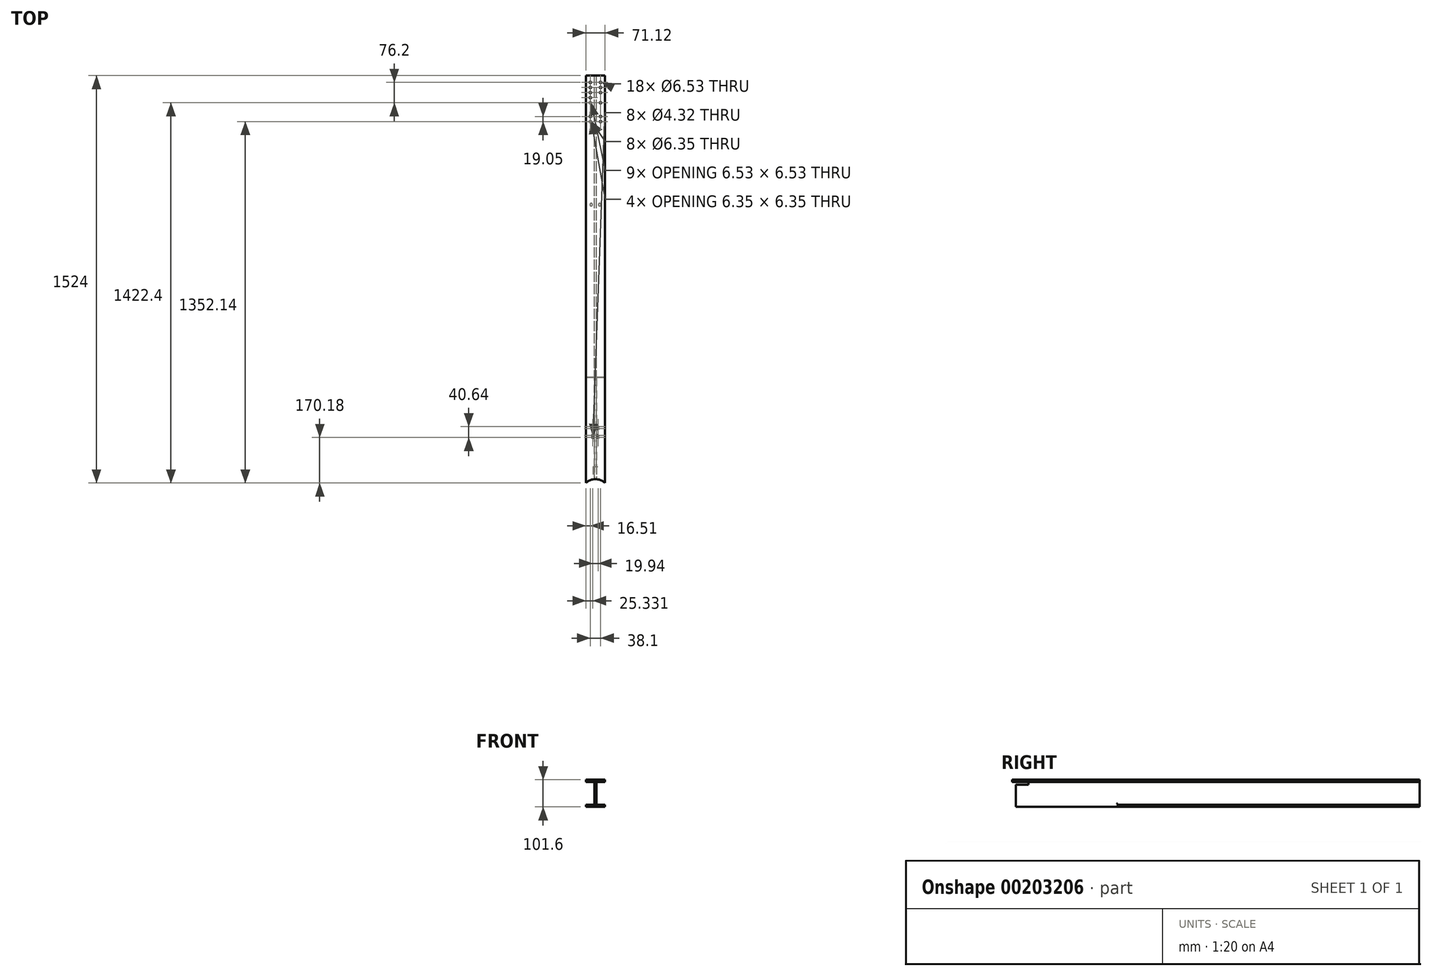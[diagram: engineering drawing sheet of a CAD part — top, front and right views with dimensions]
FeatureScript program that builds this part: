
annotation { "Feature Type Name" : "Feature", "Feature Type Description" : "" }
export const myFeature = defineFeature(function(context is Context, id is Id, definition is map)
    precondition{}
    {
        {
            var Q0;
            Q0=qCreatedBy(makeId("Front.planeOp"),FACE);
            var sketch = newSketch(context, id + "F0", { "sketchPlane" : qUnion([Q0])});
            skLineSegment(sketch, "E0.bottom", {"start": v(35.56, -50.8) * mm, "end": v(-35.56, -50.8) * mm});
            skLineSegment(sketch, "E0.top", {"start": v(35.56, 50.8) * mm, "end": v(-35.56, 50.8) * mm});
            skLineSegment(sketch, "E0.left", {"start": v(35.56, -50.8) * mm, "end": v(35.56, -42.42) * mm});
            skLineSegment(sketch, "E0.right", {"start": v(-35.56, -50.8) * mm, "end": v(-35.56, -42.42) * mm});
            skPoint(sketch, "E0.middle", {"position": v(0, 0) * mm});
            skLineSegment(sketch, "E1", {"start": v(-35.56, 50.8) * mm, "end": v(-35.56, 42.42) * mm});
            skLineSegment(sketch, "E2", {"start": v(-35.56, 42.42) * mm, "end": v(-4.2, 42.42) * mm});
            skLineSegment(sketch, "E3", {"start": v(0, 50.8) * mm, "end": v(-4.2, 50.8) * mm});
            skLineSegment(sketch, "E4", {"start": v(-4.2, 42.42) * mm, "end": v(-4.2, 0) * mm});
            skLineSegment(sketch, "E5.MirrorCS", {"start": v(4.2, 42.42) * mm, "end": v(4.2, 0) * mm});
            skLineSegment(sketch, "E6.MirrorCS", {"start": v(35.56, 50.8) * mm, "end": v(35.56, 42.42) * mm});
            skLineSegment(sketch, "E7.MirrorCS", {"start": v(-35.56, -42.42) * mm, "end": v(-4.2, -42.42) * mm});
            skLineSegment(sketch, "E8.MirrorCS", {"start": v(-4.2, -42.42) * mm, "end": v(-4.2, 0) * mm});
            skLineSegment(sketch, "E9.MirrorCS", {"start": v(4.2, -42.42) * mm, "end": v(4.2, 0) * mm});
            skPoint(sketch, "E10.orphan", {"position": v(0, -50.8) * mm});
            skLineSegment(sketch, "E11.trimOffspring", {"start": v(4.2, -42.42) * mm, "end": v(35.56, -42.42) * mm});
            skLineSegment(sketch, "E12.trimOffspring", {"start": v(4.2, 42.42) * mm, "end": v(35.56, 42.42) * mm});
            skLineSegment(sketch, "E13.trimOffspring", {"start": v(35.56, 42.42) * mm, "end": v(35.56, 50.8) * mm});
            skLineSegment(sketch, "E14.trimOffspring", {"start": v(-35.56, 42.42) * mm, "end": v(-35.56, 50.8) * mm});
            skSolve(sketch);
        }
        {
            var Q0;
            Q0=makeQuery(id+"F0.imprint","IMPRINT",FACE,{"disambiguationData":[TD([[makeQuery(id+"F0.imprint","IMPRINT",EDGE,{"derivedFrom":sQuery(id+"F0.wireOp",EDGE,"E0.bottom")}),-1.0]])]});
            extrude(context, id + "F1", {"entities" : qUnion([Q0]), "depth" : 1524 * mm});
        }
        {
            var Q0;
            Q0=makeQuery(id+"F1.opExtrude","SWEPT_EDGE",EDGE,{"disambiguationData":[OSD([sQuery(id+"F0.wireOp",EDGE,"E5.MirrorCS"),sQuery(id+"F0.wireOp",EDGE,"E12.trimOffspring")])]});
            var Q1;
            Q1=makeQuery(id+"F1.opExtrude","SWEPT_EDGE",EDGE,{"disambiguationData":[OSD([sQuery(id+"F0.wireOp",EDGE,"E9.MirrorCS"),sQuery(id+"F0.wireOp",EDGE,"E11.trimOffspring")])]});
            var Q2;
            Q2=makeQuery(id+"F1.opExtrude","SWEPT_EDGE",EDGE,{"disambiguationData":[OSD([sQuery(id+"F0.wireOp",EDGE,"E7.MirrorCS"),sQuery(id+"F0.wireOp",EDGE,"E8.MirrorCS")])]});
            var Q3;
            Q3=makeQuery(id+"F1.opExtrude","SWEPT_EDGE",EDGE,{"disambiguationData":[OSD([sQuery(id+"F0.wireOp",EDGE,"E2"),sQuery(id+"F0.wireOp",EDGE,"E4")])]});
            fillet(context, id + "F2", {"entities" : qUnion([Q0, Q1, Q2, Q3]), "radius" : 5.08 * mm, "tangentPropagation" : true, "allowEdgeOverflow" : false});
        }
        {
            var Q0;
            Q0=makeQuery(id+"F1.opExtrude","SWEPT_FACE",FACE,{"disambiguationData":[OSD([sQuery(id+"F0.wireOp",EDGE,"E0.top"),sQuery(id+"F0.wireOp",EDGE,"E3")])]});
            var sketch = newSketch(context, id + "F3", { "sketchPlane" : qUnion([Q0])});
            skLineSegment(sketch, "E15", {"start": v(0, -1524) * mm, "end": v(0, -1560.28) * mm});
            skPoint(sketch, "E15.endSnap0", {"position": v(0, -1524) * mm});
            skLineSegment(sketch, "E16", {"start": v(35.56, -1524) * mm, "end": v(0, -1560.28) * mm});
            skCircle(sketch, "E17", {"center": v(0, -1560.28) * mm, "radius": 50.8 * mm});
            skLineSegment(sketch, "E18.trimOffspring", {"start": v(0, -1611.08) * mm, "end": v(0, -1676.71) * mm});
            skSolve(sketch);
        }
        {
            var Q0;
            {var subQ6=sQuery(id+"F3.wireOp",EDGE,"E15");Q0=makeQuery(id+"F3.imprint","IMPRINT",FACE,{"disambiguationData":[TD([[makeQuery(id+"F3.imprint","IMPRINT",EDGE,{"derivedFrom":subQ6}),-1.0]])]});}
            var Q1;
            {var subQ0=sQuery(id+"F3.wireOp",EDGE,"E15");Q1=makeQuery(id+"F3.imprint","IMPRINT",FACE,{"disambiguationData":[TD([[makeQuery(id+"F3.imprint","IMPRINT",EDGE,{"derivedFrom":subQ0}),1.0]])]});}
            var Q2;
            {var subQ1=sQuery(id+"F0.wireOp",EDGE,"E0.top");var subQ2=makeQuery(id+"F1.opExtrude","CAP_EDGE",EDGE,{"disambiguationData":[OSD([subQ1,sQuery(id+"F0.wireOp",EDGE,"E3")])],"isStart":false});var subQ5=makeQuery(id+"F3.imprint","INTERSECT",VERTEX,{"derivedFrom":[subQ2,sQuery(id+"F3.wireOp",EDGE,"E15")]});Q2=makeQuery(id+"F3.imprint","IMPRINT",FACE,{"disambiguationData":[TD([[makeQuery(id+"F3.imprint","IMPRINT",EDGE,{"disambiguationData":[TD([[subQ5,-1.0]])],"derivedFrom":subQ2}),-1.0]])]});}
            extrude(context, id + "F4", {"entities" : qUnion([Q0, Q1, Q2]), "operationType" : NewBodyOperationType.REMOVE, "oppositeDirection" : true, "depth" : 101.6 * mm});
        }
        {
            var Q0;
            Q0=makeQuery(id+"F1.opExtrude","SWEPT_FACE",FACE,{"disambiguationData":[OSD([sQuery(id+"F0.wireOp",EDGE,"E5.MirrorCS"),sQuery(id+"F0.wireOp",EDGE,"E9.MirrorCS")])]});
            var sketch = newSketch(context, id + "F5", { "sketchPlane" : qUnion([Q0])});
            skSolve(sketch);
        }
        {
            var Q0;
            {var subQ0=sQuery(id+"F0.wireOp",EDGE,"E9.MirrorCS");var subQ1=sQuery(id+"F0.wireOp",EDGE,"E5.MirrorCS");Q0=makeQuery(id+"F5.imprint","IMPRINT",FACE,{"disambiguationData":[TD([[makeQuery(id+"F5.imprint","IMPRINT",EDGE,{"derivedFrom":makeQuery(id+"F1.opExtrude","CAP_EDGE",EDGE,{"disambiguationData":[OSD([subQ1,subQ0])],"isStart":true})}),1.0]])]});}
            var sketch = newSketch(context, id + "F6", { "sketchPlane" : qUnion([Q0])});
            skLineSegment(sketch, "E19", {"start": v(-1510.33, 42.42) * mm, "end": v(-1510.33, 32.26) * mm});
            skLineSegment(sketch, "E20", {"start": v(-1510.33, 32.26) * mm, "end": v(-1462.07, 32.26) * mm});
            skLineSegment(sketch, "E21", {"start": v(-1462.07, 32.26) * mm, "end": v(-1462.07, 42.42) * mm});
            skLineSegment(sketch, "E22", {"start": v(-1462.07, 42.42) * mm, "end": v(-1510.33, 42.42) * mm});
            skSolve(sketch);
        }
        {
            var Q0;
            Q0=qSketchRegion(id+"F6",true);
            extrude(context, id + "F7", {"entities" : qUnion([Q0]), "operationType" : NewBodyOperationType.REMOVE, "oppositeDirection" : true, "depth" : 25.4 * mm, "symmetric" : true});
        }
        {
            var Q0;
            Q0=makeQuery(id+"F7.boolean.opBoolean","INTERSECT",EDGE,{"derivedFrom":[makeQuery(id+"F4.boolean.opBoolean","COPY",FACE,{"derivedFrom":makeQuery(id+"F4.opExtrude","SWEPT_FACE",FACE,{"disambiguationData":[OSD([sQuery(id+"F3.wireOp",EDGE,"E17")])]})}),makeQuery(id+"F7.opExtrude","SWEPT_FACE",FACE,{"disambiguationData":[OSD([sQuery(id+"F6.wireOp",EDGE,"E20")])]})]});
            chamfer(context, id + "F8", {"entities" : qUnion([Q0]), "width" : 1.27 * mm, "tangentPropagation" : true});
        }
        {
            var Q0;
            Q0=makeQuery(id+"F1.opExtrude","SWEPT_FACE",FACE,{"disambiguationData":[OSD([sQuery(id+"F0.wireOp",EDGE,"E0.top"),sQuery(id+"F0.wireOp",EDGE,"E3")])]});
            var sketch = newSketch(context, id + "F9", { "sketchPlane" : qUnion([Q0])});
            skLineSegment(sketch, "E23", {"start": v(-0.26, -1524) * mm, "end": v(-0.26, -0.03) * mm});
            skLineSegment(sketch, "E24.bottom", {"start": v(9.71, -1353.82) * mm, "end": v(-10.23, -1353.82) * mm});
            skLineSegment(sketch, "E24.top", {"start": v(9.71, -1313.18) * mm, "end": v(-10.23, -1313.18) * mm});
            skLineSegment(sketch, "E25.bottom", {"start": v(9.71, -1346.2) * mm, "end": v(-10.23, -1346.2) * mm});
            skLineSegment(sketch, "E25.top", {"start": v(9.71, -1320.8) * mm, "end": v(-10.23, -1320.8) * mm});
            skLineSegment(sketch, "E26", {"start": v(35.56, -1524) * mm, "end": v(-35.56, -1524) * mm});
            skLineSegment(sketch, "E27", {"start": v(-0.26, -1524) * mm, "end": v(-0.26, -1353.82) * mm});
            skLineSegment(sketch, "E28", {"start": v(-0.26, -1353.82) * mm, "end": v(-0.26, -1346.2) * mm});
            skLineSegment(sketch, "E29", {"start": v(-0.26, -1346.2) * mm, "end": v(-0.26, -1320.8) * mm});
            skLineSegment(sketch, "E30", {"start": v(-0.26, -1320.8) * mm, "end": v(-0.26, -1313.18) * mm});
            skSolve(sketch);
        }
        {
            var Q0;
            Q0=sQuery(id+"F9.wireOp",VERTEX,"E24.bottom.end");
            var Q1;
            Q1=sQuery(id+"F9.wireOp",VERTEX,"E25.bottom.end");
            var Q2;
            Q2=sQuery(id+"F9.wireOp",VERTEX,"E25.top.end");
            var Q3;
            Q3=sQuery(id+"F9.wireOp",VERTEX,"E24.top.end");
            var Q4;
            Q4=sQuery(id+"F9.wireOp",VERTEX,"E24.top.start");
            var Q5;
            Q5=sQuery(id+"F9.wireOp",VERTEX,"E25.top.start");
            var Q6;
            Q6=sQuery(id+"F9.wireOp",VERTEX,"E25.bottom.start");
            var Q7;
            Q7=sQuery(id+"F9.wireOp",VERTEX,"E24.bottom.start");
            var Q8;
            Q8=makeQuery(id+"F1.opExtrude","SWEPT_BODY",BODY,{"disambiguationData":[OSD([sQuery(id+"F0.wireOp",EDGE,"E0.bottom"),sQuery(id+"F0.wireOp",EDGE,"E0.top"),sQuery(id+"F0.wireOp",EDGE,"E0.left"),sQuery(id+"F0.wireOp",EDGE,"E0.right"),sQuery(id+"F0.wireOp",EDGE,"E2"),sQuery(id+"F0.wireOp",EDGE,"E3"),sQuery(id+"F0.wireOp",EDGE,"E4"),sQuery(id+"F0.wireOp",EDGE,"E5.MirrorCS"),sQuery(id+"F0.wireOp",EDGE,"E7.MirrorCS"),sQuery(id+"F0.wireOp",EDGE,"E8.MirrorCS"),sQuery(id+"F0.wireOp",EDGE,"E9.MirrorCS"),sQuery(id+"F0.wireOp",EDGE,"E11.trimOffspring"),sQuery(id+"F0.wireOp",EDGE,"E12.trimOffspring"),sQuery(id+"F0.wireOp",EDGE,"E13.trimOffspring"),sQuery(id+"F0.wireOp",EDGE,"E14.trimOffspring")])]});
            hole(context, id + "F10", {"style" : HoleStyle.SIMPLE, "endStyle" : HoleEndStyle.BLIND, "standardTappedOrClearance" : lookupTablePath({ "standard" : "ANSI", "fit" : "Close", "size" : "#8", "type" : "Clearance" }), "standardBlindInLast" : lookupTablePath({ "fit" : "Close", "standard" : "ANSI", "size" : "#8", "type" : "Clearance" }), "holeDiameter" : 4.32 * mm, "holeDepth" : 25.4 * mm, "locations" : qUnion([Q0, Q1, Q2, Q3, Q4, Q5, Q6, Q7]), "scope" : qUnion([Q8])});
        }
        {
            var Q0;
            Q0=makeQuery(id+"F1.opExtrude","SWEPT_FACE",FACE,{"disambiguationData":[OSD([sQuery(id+"F0.wireOp",EDGE,"E0.bottom")])]});
            var sketch = newSketch(context, id + "F11", { "sketchPlane" : qUnion([Q0])});
            skLineSegment(sketch, "E31", {"start": v(4.2, 1509.65) * mm, "end": v(4.2, 1128.65) * mm});
            skLineSegment(sketch, "E32.bottom", {"start": v(4.2, 1128.65) * mm, "end": v(39.68, 1128.65) * mm});
            skLineSegment(sketch, "E32.top", {"start": v(4.2, 1528.41) * mm, "end": v(39.68, 1528.41) * mm});
            skLineSegment(sketch, "E32.left", {"start": v(4.2, 1128.65) * mm, "end": v(4.2, 1528.41) * mm});
            skLineSegment(sketch, "E32.right", {"start": v(39.68, 1128.65) * mm, "end": v(39.68, 1528.41) * mm});
            skLineSegment(sketch, "E33", {"start": v(0, 1526.52) * mm, "end": v(0, 1517.43) * mm});
            skLineSegment(sketch, "E34.MirrorCS", {"start": v(-4.2, 1528.41) * mm, "end": v(-39.68, 1528.41) * mm});
            skLineSegment(sketch, "E35.MirrorCS", {"start": v(-39.68, 1128.65) * mm, "end": v(-39.68, 1528.41) * mm});
            skLineSegment(sketch, "E36.MirrorCS", {"start": v(-4.2, 1128.65) * mm, "end": v(-4.2, 1528.41) * mm});
            skLineSegment(sketch, "E37.MirrorCS", {"start": v(-4.2, 1128.65) * mm, "end": v(-39.68, 1128.65) * mm});
            skSolve(sketch);
        }
        {
            var Q0;
            Q0=qSketchRegion(id+"F11",true);
            extrude(context, id + "F12", {"entities" : qUnion([Q0]), "operationType" : NewBodyOperationType.REMOVE, "oppositeDirection" : true, "depth" : 25.4 * mm});
        }
        {
            var Q0;
            Q0=makeQuery(id+"F12.boolean.opBoolean","COPY",EDGE,{"derivedFrom":makeQuery(id+"F12.opExtrude","SWEPT_EDGE",EDGE,{"disambiguationData":[OSD([sQuery(id+"F11.wireOp",EDGE,"E32.bottom"),sQuery(id+"F11.wireOp",EDGE,"E32.left")])]})});
            var Q1;
            Q1=makeQuery(id+"F12.boolean.opBoolean","COPY",EDGE,{"derivedFrom":makeQuery(id+"F12.opExtrude","SWEPT_EDGE",EDGE,{"disambiguationData":[OSD([sQuery(id+"F11.wireOp",EDGE,"E36.MirrorCS"),sQuery(id+"F11.wireOp",EDGE,"E37.MirrorCS")])]})});
            fillet(context, id + "F13", {"entities" : qUnion([Q0, Q1]), "radius" : 3.17 * mm, "tangentPropagation" : true, "allowEdgeOverflow" : false});
        }
        {
            var Q0;
            Q0=makeQuery(id+"F1.opExtrude","SWEPT_FACE",FACE,{"disambiguationData":[OSD([sQuery(id+"F0.wireOp",EDGE,"E0.bottom")])]});
            var sketch = newSketch(context, id + "F14", { "sketchPlane" : qUnion([Q0])});
            skLineSegment(sketch, "E38", {"start": v(0, 0) * mm, "end": v(0, 482.6) * mm});
            skPoint(sketch, "E38.endSnap0", {"position": v(0, 0) * mm});
            skLineSegment(sketch, "E39", {"start": v(0, 482.6) * mm, "end": v(15.88, 482.6) * mm});
            skLineSegment(sketch, "E40", {"start": v(15.88, 482.6) * mm, "end": v(-15.88, 482.6) * mm});
            skSolve(sketch);
        }
        {
            var Q0;
            Q0=sQuery(id+"F14.wireOp",VERTEX,"E40.start");
            var Q1;
            Q1=sQuery(id+"F14.wireOp",VERTEX,"E40.end");
            var Q2;
            Q2=makeQuery(id+"F1.opExtrude","SWEPT_BODY",BODY,{"disambiguationData":[OSD([sQuery(id+"F0.wireOp",EDGE,"E0.bottom"),sQuery(id+"F0.wireOp",EDGE,"E0.top"),sQuery(id+"F0.wireOp",EDGE,"E0.left"),sQuery(id+"F0.wireOp",EDGE,"E0.right"),sQuery(id+"F0.wireOp",EDGE,"E2"),sQuery(id+"F0.wireOp",EDGE,"E3"),sQuery(id+"F0.wireOp",EDGE,"E4"),sQuery(id+"F0.wireOp",EDGE,"E5.MirrorCS"),sQuery(id+"F0.wireOp",EDGE,"E7.MirrorCS"),sQuery(id+"F0.wireOp",EDGE,"E8.MirrorCS"),sQuery(id+"F0.wireOp",EDGE,"E9.MirrorCS"),sQuery(id+"F0.wireOp",EDGE,"E11.trimOffspring"),sQuery(id+"F0.wireOp",EDGE,"E12.trimOffspring"),sQuery(id+"F0.wireOp",EDGE,"E13.trimOffspring"),sQuery(id+"F0.wireOp",EDGE,"E14.trimOffspring")])]});
            hole(context, id + "F15", {"style" : HoleStyle.SIMPLE, "endStyle" : HoleEndStyle.BLIND, "standardTappedOrClearance" : lookupTablePath({ "standard" : "ANSI", "fit" : "Close", "size" : "3/8", "type" : "Clearance" }), "standardBlindInLast" : lookupTablePath({ "fit" : "Close", "standard" : "ANSI", "size" : "3/8", "type" : "Clearance" }), "holeDiameter" : 9.8 * mm, "holeDepth" : 25.4 * mm, "locations" : qUnion([Q0, Q1]), "scope" : qUnion([Q2])});
        }
        {
            var Q0;
            Q0=makeQuery(id+"F1.opExtrude","SWEPT_FACE",FACE,{"disambiguationData":[OSD([sQuery(id+"F0.wireOp",EDGE,"E0.top"),sQuery(id+"F0.wireOp",EDGE,"E3")])]});
            var sketch = newSketch(context, id + "F16", { "sketchPlane" : qUnion([Q0])});
            skLineSegment(sketch, "E41", {"start": v(0, 0) * mm, "end": v(0, -25.4) * mm});
            skLineSegment(sketch, "E42", {"start": v(0, -25.4) * mm, "end": v(19.05, -25.4) * mm});
            skLineSegment(sketch, "E43", {"start": v(19.05, -25.4) * mm, "end": v(19.05, -44.45) * mm});
            skLineSegment(sketch, "E44", {"start": v(19.05, -44.45) * mm, "end": v(19.05, -63.5) * mm});
            skLineSegment(sketch, "E45", {"start": v(19.05, -63.5) * mm, "end": v(19.05, -82.55) * mm});
            skLineSegment(sketch, "E46", {"start": v(19.05, -82.55) * mm, "end": v(19.05, -101.6) * mm});
            skLineSegment(sketch, "E47.MirrorCS", {"start": v(-19.05, -25.4) * mm, "end": v(-19.05, -44.45) * mm});
            skLineSegment(sketch, "E48.MirrorCS", {"start": v(-19.05, -44.45) * mm, "end": v(-19.05, -63.5) * mm});
            skLineSegment(sketch, "E49.MirrorCS", {"start": v(-19.05, -63.5) * mm, "end": v(-19.05, -82.55) * mm});
            skLineSegment(sketch, "E50.MirrorCS", {"start": v(-19.05, -82.55) * mm, "end": v(-19.05, -101.6) * mm});
            skLineSegment(sketch, "E51.MirrorCS", {"start": v(0, -25.4) * mm, "end": v(-19.05, -25.4) * mm});
            skSolve(sketch);
        }
        {
            var Q0;
            Q0=sQuery(id+"F16.wireOp",VERTEX,"E50.MirrorCS.start");
            var Q1;
            Q1=sQuery(id+"F16.wireOp",VERTEX,"E50.MirrorCS.end");
            var Q2;
            Q2=sQuery(id+"F16.wireOp",VERTEX,"E49.MirrorCS.start");
            var Q3;
            Q3=sQuery(id+"F16.wireOp",VERTEX,"E48.MirrorCS.start");
            var Q4;
            Q4=sQuery(id+"F16.wireOp",VERTEX,"E51.MirrorCS.end");
            var Q5;
            Q5=sQuery(id+"F16.wireOp",VERTEX,"E43.start");
            var Q6;
            Q6=sQuery(id+"F16.wireOp",VERTEX,"E44.start");
            var Q7;
            Q7=sQuery(id+"F16.wireOp",VERTEX,"E45.start");
            var Q8;
            Q8=sQuery(id+"F16.wireOp",VERTEX,"E46.end");
            var Q9;
            Q9=sQuery(id+"F16.wireOp",VERTEX,"E46.end");
            var Q10;
            Q10=makeQuery(id+"F1.opExtrude","SWEPT_BODY",BODY,{"disambiguationData":[OSD([sQuery(id+"F0.wireOp",EDGE,"E0.bottom"),sQuery(id+"F0.wireOp",EDGE,"E0.top"),sQuery(id+"F0.wireOp",EDGE,"E0.left"),sQuery(id+"F0.wireOp",EDGE,"E0.right"),sQuery(id+"F0.wireOp",EDGE,"E2"),sQuery(id+"F0.wireOp",EDGE,"E3"),sQuery(id+"F0.wireOp",EDGE,"E4"),sQuery(id+"F0.wireOp",EDGE,"E5.MirrorCS"),sQuery(id+"F0.wireOp",EDGE,"E7.MirrorCS"),sQuery(id+"F0.wireOp",EDGE,"E8.MirrorCS"),sQuery(id+"F0.wireOp",EDGE,"E9.MirrorCS"),sQuery(id+"F0.wireOp",EDGE,"E11.trimOffspring"),sQuery(id+"F0.wireOp",EDGE,"E12.trimOffspring"),sQuery(id+"F0.wireOp",EDGE,"E13.trimOffspring"),sQuery(id+"F0.wireOp",EDGE,"E14.trimOffspring")])]});
            hole(context, id + "F17", {"style" : HoleStyle.SIMPLE, "endStyle" : HoleEndStyle.THROUGH, "standardTappedOrClearance" : lookupTablePath({ "standard" : "ANSI", "fit" : "Close", "size" : "1/4", "type" : "Clearance" }), "standardBlindInLast" : lookupTablePath({ "fit" : "Close", "standard" : "ANSI", "size" : "1/4", "type" : "Clearance" }), "holeDiameter" : 6.53 * mm, "locations" : qUnion([Q0, Q1, Q2, Q3, Q4, Q5, Q6, Q7, Q8, Q9]), "scope" : qUnion([Q10]), "isTappedThrough" : true});
        }
        {
            var Q0;
            Q0=makeQuery(id+"F1.opExtrude","SWEPT_FACE",FACE,{"disambiguationData":[OSD([sQuery(id+"F0.wireOp",EDGE,"E0.top"),sQuery(id+"F0.wireOp",EDGE,"E3")])]});
            var sketch = newSketch(context, id + "F18", { "sketchPlane" : qUnion([Q0])});
            skLineSegment(sketch, "E52", {"start": v(-19.05, -101.6) * mm, "end": v(-19.05, -152.8) * mm});
            skLineSegment(sketch, "E53", {"start": v(-19.05, -152.8) * mm, "end": v(-19.05, -171.86) * mm});
            skLineSegment(sketch, "E54", {"start": v(-19.05, -171.86) * mm, "end": v(-19.05, -190.9) * mm});
            skLineSegment(sketch, "E55", {"start": v(-19.05, -190.9) * mm, "end": v(19.05, -190.9) * mm});
            skLineSegment(sketch, "E56", {"start": v(19.05, -190.9) * mm, "end": v(19.05, -171.86) * mm});
            skLineSegment(sketch, "E57", {"start": v(19.05, -171.86) * mm, "end": v(19.05, -152.8) * mm});
            skSolve(sketch);
        }
        {
            var Q0;
            Q0=sQuery(id+"F18.wireOp",VERTEX,"E53.start");
            var Q1;
            Q1=sQuery(id+"F18.wireOp",VERTEX,"E54.start");
            var Q2;
            Q2=sQuery(id+"F18.wireOp",VERTEX,"E57.end");
            var Q3;
            Q3=sQuery(id+"F18.wireOp",VERTEX,"E57.start");
            var Q4;
            Q4=makeQuery(id+"F1.opExtrude","SWEPT_BODY",BODY,{"disambiguationData":[OSD([sQuery(id+"F0.wireOp",EDGE,"E0.bottom"),sQuery(id+"F0.wireOp",EDGE,"E0.top"),sQuery(id+"F0.wireOp",EDGE,"E0.left"),sQuery(id+"F0.wireOp",EDGE,"E0.right"),sQuery(id+"F0.wireOp",EDGE,"E2"),sQuery(id+"F0.wireOp",EDGE,"E3"),sQuery(id+"F0.wireOp",EDGE,"E4"),sQuery(id+"F0.wireOp",EDGE,"E5.MirrorCS"),sQuery(id+"F0.wireOp",EDGE,"E7.MirrorCS"),sQuery(id+"F0.wireOp",EDGE,"E8.MirrorCS"),sQuery(id+"F0.wireOp",EDGE,"E9.MirrorCS"),sQuery(id+"F0.wireOp",EDGE,"E11.trimOffspring"),sQuery(id+"F0.wireOp",EDGE,"E12.trimOffspring"),sQuery(id+"F0.wireOp",EDGE,"E13.trimOffspring"),sQuery(id+"F0.wireOp",EDGE,"E14.trimOffspring")])]});
            hole(context, id + "F19", {"style" : HoleStyle.SIMPLE, "endStyle" : HoleEndStyle.THROUGH, "holeDiameter" : 6.35 * mm, "locations" : qUnion([Q0, Q1, Q2, Q3]), "scope" : qUnion([Q4]), "isTappedThrough" : true});
        }
    });
